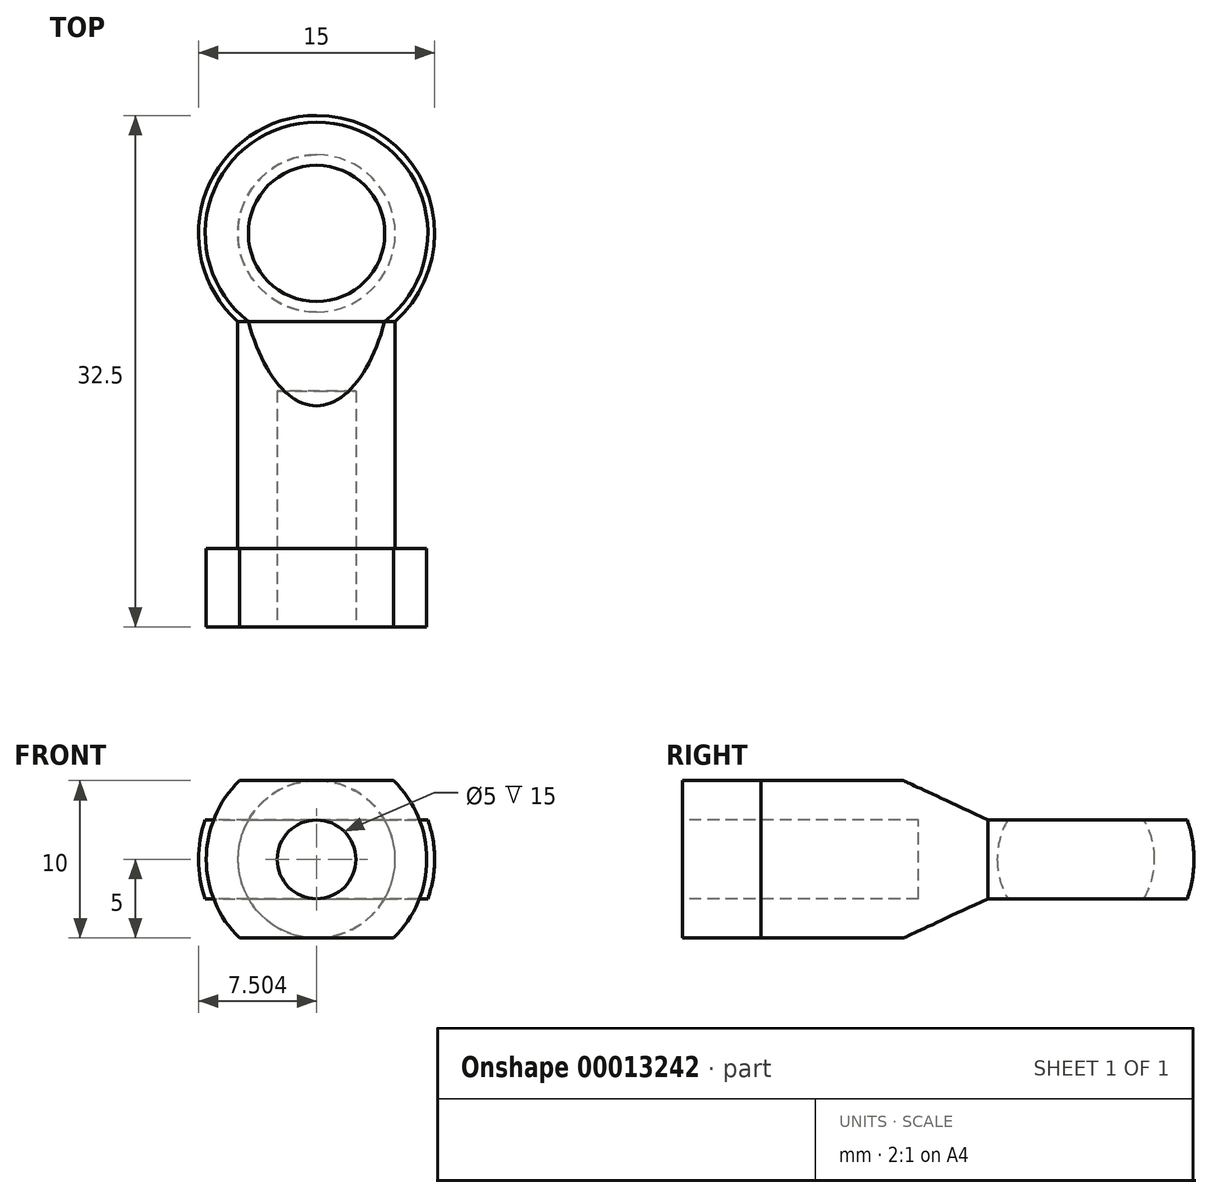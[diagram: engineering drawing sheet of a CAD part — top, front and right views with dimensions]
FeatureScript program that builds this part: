
annotation { "Feature Type Name" : "Feature", "Feature Type Description" : "" }
export const myFeature = defineFeature(function(context is Context, id is Id, definition is map)
    precondition{}
    {
        {
            var Q0;
            Q0=qCreatedBy(makeId("Top.planeOp"),FACE);
            var sketch = newSketch(context, id + "F0", { "sketchPlane" : qUnion([Q0])});
            skCircle(sketch, "E0", {"center": v(-12, 1.28) * mm, "radius": 5 * mm});
            skCircle(sketch, "E1", {"center": v(-12, 1.28) * mm, "radius": 2.5 * mm});
            skLineSegment(sketch, "E2", {"start": v(-12, 6.28) * mm, "end": v(-12, -3.72) * mm});
            skCircle(sketch, "E3", {"center": v(18.13, 9.1) * mm, "radius": 4 * mm});
            skLineSegment(sketch, "E4", {"start": v(13.13, 3.5) * mm, "end": v(23.13, 3.5) * mm, "construction": true});
            skArc(sketch, "E5", {"start": v(13.13, 3.5) * mm, "mid": v(18.13, 1.6) * mm, "end": v(23.13, 3.5) * mm, "construction": true});
            skArc(sketch, "E6", {"start": v(23.13, 3.5) * mm, "mid": v(18.13, 16.6) * mm, "end": v(13.13, 3.5) * mm});
            skLineSegment(sketch, "E7", {"start": v(13.13, 3.5) * mm, "end": v(13.13, -15.9) * mm});
            skLineSegment(sketch, "E8", {"start": v(13.13, -15.9) * mm, "end": v(23.13, -15.9) * mm});
            skLineSegment(sketch, "E9", {"start": v(23.13, -15.9) * mm, "end": v(23.13, 3.5) * mm});
            skLineSegment(sketch, "E10.bottom", {"start": v(11.13, -15.9) * mm, "end": v(25.13, -15.9) * mm});
            skLineSegment(sketch, "E10.top", {"start": v(11.13, -10.9) * mm, "end": v(25.13, -10.9) * mm});
            skLineSegment(sketch, "E10.left", {"start": v(11.13, -15.9) * mm, "end": v(11.13, -10.9) * mm});
            skLineSegment(sketch, "E10.right", {"start": v(25.13, -15.9) * mm, "end": v(25.13, -10.9) * mm});
            skLineSegment(sketch, "E11", {"start": v(18.13, 16.6) * mm, "end": v(18.13, -15.9) * mm});
            skCircle(sketch, "E12", {"center": v(18.13, 9.1) * mm, "radius": 5 * mm});
            skSolve(sketch);
        }
        {
            var Q0;
            {var subQ0=sQuery(id+"F0.wireOp",EDGE,"E2");var subQ3=sQuery(id+"F0.wireOp",EDGE,"E0");var subQ6=makeQuery(id+"F0.imprint","INTERSECT",VERTEX,{"disambiguationData":[OD(0.0)],"derivedFrom":[subQ3,subQ0]});Q0=makeQuery(id+"F0.imprint","IMPRINT",FACE,{"disambiguationData":[TD([[makeQuery(id+"F0.imprint","IMPRINT",EDGE,{"disambiguationData":[TD([[subQ6,1.0]])],"derivedFrom":subQ3}),1.0]])]});}
            var Q1;
            {var subQ0=sQuery(id+"F0.wireOp",EDGE,"E2");var subQ1=sQuery(id+"F0.wireOp",EDGE,"E1");var subQ3=makeQuery(id+"F0.imprint","INTERSECT",VERTEX,{"disambiguationData":[OD(0.0)],"derivedFrom":[subQ1,subQ0]});Q1=makeQuery(id+"F0.imprint","IMPRINT",FACE,{"disambiguationData":[TD([[makeQuery(id+"F0.imprint","IMPRINT",EDGE,{"disambiguationData":[TD([[subQ3,1.0]])],"derivedFrom":subQ1}),1.0]])]});}
            var Q2;
            Q2=sQuery(id+"F0.wireOp",EDGE,"E2");
            revolve(context, id + "F1", {"entities" : qUnion([Q0, Q1]), "axis" : qUnion([Q2]), "revolveType" : RevolveType.FULL});
        }
        {
            var Q0;
            {var subQ0=sQuery(id+"F0.wireOp",EDGE,"E2");var subQ1=sQuery(id+"F0.wireOp",EDGE,"E1");var subQ3=makeQuery(id+"F0.imprint","INTERSECT",VERTEX,{"disambiguationData":[OD(0.0)],"derivedFrom":[subQ1,subQ0]});Q0=makeQuery(id+"F0.imprint","IMPRINT",FACE,{"disambiguationData":[TD([[makeQuery(id+"F0.imprint","IMPRINT",EDGE,{"disambiguationData":[TD([[subQ3,-1.0]])],"derivedFrom":subQ1}),1.0]])]});}
            var Q1;
            {var subQ0=sQuery(id+"F0.wireOp",EDGE,"E2");var subQ1=sQuery(id+"F0.wireOp",EDGE,"E1");var subQ3=makeQuery(id+"F0.imprint","INTERSECT",VERTEX,{"disambiguationData":[OD(0.0)],"derivedFrom":[subQ1,subQ0]});Q1=makeQuery(id+"F0.imprint","IMPRINT",FACE,{"disambiguationData":[TD([[makeQuery(id+"F0.imprint","IMPRINT",EDGE,{"disambiguationData":[TD([[subQ3,1.0]])],"derivedFrom":subQ1}),1.0]])]});}
            extrude(context, id + "F2", {"entities" : qUnion([Q0, Q1]), "operationType" : NewBodyOperationType.REMOVE, "endBound" : BoundingType.SYMMETRIC, "oppositeDirection" : true, "depth" : 10 * mm});
        }
        {
            var Q0;
            Q0=makeQuery(id+"F2.boolean.opBoolean","INTERSECT",EDGE,{"disambiguationData":[OD(1.0)],"derivedFrom":[makeQuery(id+"F1.opRevolve","SWEPT_FACE",FACE,{"disambiguationData":[OSD([sQuery(id+"F0.wireOp",EDGE,"E0")])]}),makeQuery(id+"F2.opExtrude","SWEPT_FACE",FACE,{"disambiguationData":[OSD([sQuery(id+"F0.wireOp",EDGE,"E1")])]})]});
            var Q1;
            Q1=makeQuery(id+"F2.boolean.opBoolean","INTERSECT",EDGE,{"disambiguationData":[OD(0.0)],"derivedFrom":[makeQuery(id+"F1.opRevolve","SWEPT_FACE",FACE,{"disambiguationData":[OSD([sQuery(id+"F0.wireOp",EDGE,"E0")])]}),makeQuery(id+"F2.opExtrude","SWEPT_FACE",FACE,{"disambiguationData":[OSD([sQuery(id+"F0.wireOp",EDGE,"E1")])]})]});
            chamfer(context, id + "F3", {"entities" : qUnion([Q0, Q1]), "chamferType" : ChamferType.OFFSET_ANGLE, "width" : .6 * mm, "oppositeDirection" : true, "angle" : 90 * degree, "tangentPropagation" : true});
        }
        {
            var Q0;
            {var subQ3=sQuery(id+"F0.wireOp",EDGE,"E10.bottom");var subQ5=sQuery(id+"F0.wireOp",EDGE,"E9");var subQ7=makeQuery(id+"F0.imprint","INTERSECT",VERTEX,{"derivedFrom":[subQ5,subQ3]});Q0=makeQuery(id+"F0.imprint","IMPRINT",FACE,{"disambiguationData":[TD([[makeQuery(id+"F0.imprint","IMPRINT",EDGE,{"disambiguationData":[TD([[subQ7,-1.0]])],"derivedFrom":subQ5}),1.0]])]});}
            var Q1;
            {var subQ0=sQuery(id+"F0.wireOp",EDGE,"E10.right");Q1=makeQuery(id+"F0.imprint","IMPRINT",FACE,{"disambiguationData":[TD([[makeQuery(id+"F0.imprint","IMPRINT",EDGE,{"derivedFrom":subQ0}),1.0]])]});}
            var Q2;
            {var subQ6=sQuery(id+"F0.wireOp",EDGE,"E6");var subQ8=sQuery(id+"F0.wireOp",EDGE,"E9");var subQ10=makeQuery(id+"F0.imprint","INTERSECT",VERTEX,{"derivedFrom":[subQ6,subQ8]});Q2=makeQuery(id+"F0.imprint","IMPRINT",FACE,{"disambiguationData":[TD([[makeQuery(id+"F0.imprint","IMPRINT",EDGE,{"disambiguationData":[TD([[subQ10,-1.0]])],"derivedFrom":subQ6}),1.0]])]});}
            var Q3;
            Q3=sQuery(id+"F0.wireOp",EDGE,"E11");
            revolve(context, id + "F4", {"entities" : qUnion([Q0, Q1, Q2]), "axis" : qUnion([Q3]), "revolveType" : RevolveType.FULL});
        }
        {
            var Q0;
            {var subQ0=sQuery(id+"F0.wireOp",EDGE,"E11");var subQ1=sQuery(id+"F0.wireOp",EDGE,"E3");var subQ3=makeQuery(id+"F0.imprint","INTERSECT",VERTEX,{"disambiguationData":[OD(0.0)],"derivedFrom":[subQ1,subQ0]});Q0=makeQuery(id+"F0.imprint","IMPRINT",FACE,{"disambiguationData":[TD([[makeQuery(id+"F0.imprint","IMPRINT",EDGE,{"disambiguationData":[TD([[subQ3,-1.0]])],"derivedFrom":subQ1}),1.0]])]});}
            var Q1;
            {var subQ0=sQuery(id+"F0.wireOp",EDGE,"E11");var subQ1=sQuery(id+"F0.wireOp",EDGE,"E3");var subQ3=makeQuery(id+"F0.imprint","INTERSECT",VERTEX,{"disambiguationData":[OD(0.0)],"derivedFrom":[subQ1,subQ0]});Q1=makeQuery(id+"F0.imprint","IMPRINT",FACE,{"disambiguationData":[TD([[makeQuery(id+"F0.imprint","IMPRINT",EDGE,{"disambiguationData":[TD([[subQ3,1.0]])],"derivedFrom":subQ1}),1.0]])]});}
            extrude(context, id + "F5", {"entities" : qUnion([Q0, Q1]), "operationType" : NewBodyOperationType.REMOVE, "endBound" : BoundingType.SYMMETRIC, "oppositeDirection" : true, "depth" : 15 * mm});
        }
        {
            var Q0;
            Q0=qCreatedBy(makeId("Right.planeOp"),FACE);
            var sketch = newSketch(context, id + "F6", { "sketchPlane" : qUnion([Q0])});
            skLineSegment(sketch, "E13.0", {"start": v(16.6, 0) * mm, "end": v(-15.9, 0) * mm});
            skPoint(sketch, "E13.1", {"position": v(16.6, 0) * mm});
            skPoint(sketch, "E14.0", {"position": v(9.1, 0) * mm});
            skPoint(sketch, "E14.1", {"position": v(3.5, 0) * mm});
            skPoint(sketch, "E14.2", {"position": v(-10.9, 0) * mm});
            skPoint(sketch, "E14.3", {"position": v(-15.9, 0) * mm});
            skLineSegment(sketch, "E15", {"start": v(-10.9, 5) * mm, "end": v(-10.9, -5) * mm, "construction": true});
            skLineSegment(sketch, "E16", {"start": v(3.5, 2.5) * mm, "end": v(3.5, -2.5) * mm, "construction": true});
            skLineSegment(sketch, "E17", {"start": v(16.6, 2.5) * mm, "end": v(16.6, -2.5) * mm});
            skLineSegment(sketch, "E18", {"start": v(-15.9, 5) * mm, "end": v(-15.9, -5) * mm});
            skLineSegment(sketch, "E19", {"start": v(16.6, 2.5) * mm, "end": v(3.5, 2.5) * mm});
            skLineSegment(sketch, "E20", {"start": v(16.6, -2.5) * mm, "end": v(3.5, -2.5) * mm});
            skLineSegment(sketch, "E21", {"start": v(-10.9, 5) * mm, "end": v(-15.9, 5) * mm});
            skLineSegment(sketch, "E22", {"start": v(-10.9, -5) * mm, "end": v(-15.9, -5) * mm});
            skLineSegment(sketch, "E23", {"start": v(-10.9, 5) * mm, "end": v(-1.86, 5) * mm});
            skLineSegment(sketch, "E24", {"start": v(-1.86, 5) * mm, "end": v(3.5, 2.5) * mm});
            skLineSegment(sketch, "E25", {"start": v(3.5, -2.5) * mm, "end": v(-1.86, -5) * mm});
            skLineSegment(sketch, "E26", {"start": v(-1.86, -5) * mm, "end": v(-10.9, -5) * mm});
            skSolve(sketch);
        }
        {
            var Q0;
            {var subQ3=sQuery(id+"F6.wireOp",EDGE,"E13.0");Q0=makeQuery(id+"F6.imprint","IMPRINT",FACE,{"disambiguationData":[TD([[makeQuery(id+"F6.imprint","IMPRINT",EDGE,{"derivedFrom":subQ3}),-1.0]])]});}
            var Q1;
            {var subQ3=sQuery(id+"F6.wireOp",EDGE,"E13.0");Q1=makeQuery(id+"F6.imprint","IMPRINT",FACE,{"disambiguationData":[TD([[makeQuery(id+"F6.imprint","IMPRINT",EDGE,{"derivedFrom":subQ3}),1.0]])]});}
            extrude(context, id + "F7", {"entities" : qUnion([Q0, Q1]), "operationType" : NewBodyOperationType.INTERSECT, "depth" : 30 * mm});
        }
        {
            var Q0;
            Q0=makeQuery(id+"F4.opRevolve","SWEPT_FACE",FACE,{"disambiguationData":[OSD([sQuery(id+"F0.wireOp",EDGE,"E10.bottom")])]});
            var sketch = newSketch(context, id + "F8", { "sketchPlane" : qUnion([Q0])});
            skArc(sketch, "E27.0", {"start": v(23.03, 5) * mm, "mid": v(25.13, 0) * mm, "end": v(23.03, -5) * mm});
            skArc(sketch, "E28.0", {"start": v(13.24, -5) * mm, "mid": v(11.13, 0) * mm, "end": v(13.24, 5) * mm});
            skLineSegment(sketch, "E29.0", {"start": v(23.03, 5) * mm, "end": v(13.24, 5) * mm});
            skLineSegment(sketch, "E30.0", {"start": v(23.03, -5) * mm, "end": v(13.24, -5) * mm});
            skCircle(sketch, "E31", {"center": v(18.13, 0) * mm, "radius": 2.5 * mm});
            skSolve(sketch);
        }
        {
            var Q0;
            Q0=makeQuery(id+"F8.imprint","IMPRINT",FACE,{"disambiguationData":[TD([[makeQuery(id+"F8.imprint","IMPRINT",EDGE,{"derivedFrom":sQuery(id+"F8.wireOp",EDGE,"E31")}),1.0]])]});
            extrude(context, id + "F9", {"entities" : qUnion([Q0]), "operationType" : NewBodyOperationType.REMOVE, "oppositeDirection" : true, "depth" : 15 * mm});
        }
    });
